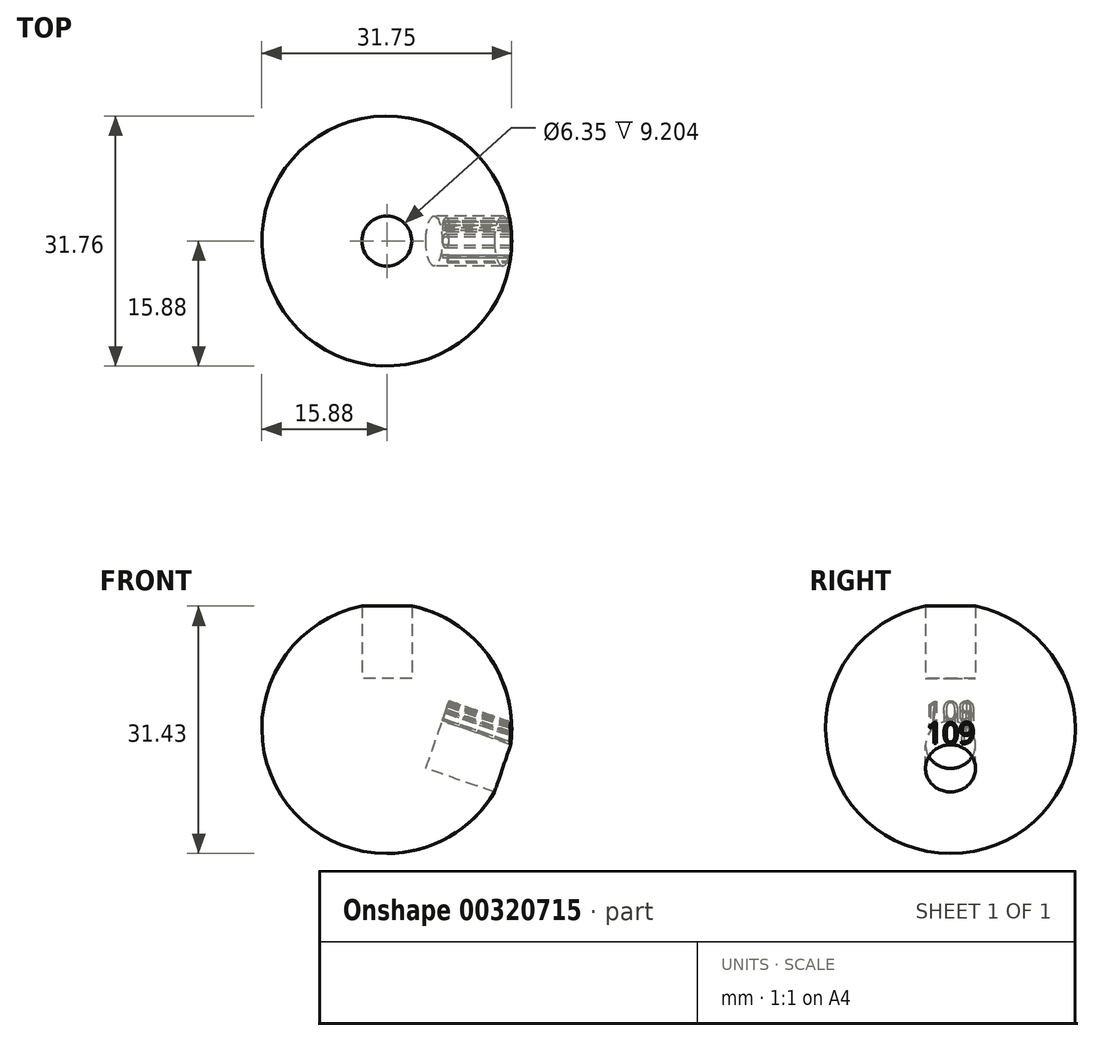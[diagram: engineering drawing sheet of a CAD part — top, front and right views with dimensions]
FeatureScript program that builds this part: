
annotation { "Feature Type Name" : "Feature", "Feature Type Description" : "" }
export const myFeature = defineFeature(function(context is Context, id is Id, definition is map)
    precondition{}
    {
        {
            var Q0;
            Q0=qCreatedBy(makeId("Front.planeOp"),FACE);
            var sketch = newSketch(context, id + "F0", { "sketchPlane" : qUnion([Q0])});
            skArc(sketch, "E0", {"start": v(0, 15.88) * mm, "mid": v(-15.88, 0) * mm, "end": v(0, -15.88) * mm});
            skLineSegment(sketch, "E1", {"start": v(0, 15.88) * mm, "end": v(0, -15.88) * mm});
            skSolve(sketch);
        }
        {
            var Q0;
            Q0=qCreatedBy(makeId("Top.planeOp"),FACE);
            var sketch = newSketch(context, id + "F1", { "sketchPlane" : qUnion([Q0])});
            skCircle(sketch, "E2", {"center": v(0, 0) * mm, "radius": 0.5 * mm});
            skCircle(sketch, "E3", {"center": v(0, 0) * mm, "radius": 15.88 * mm});
            skSolve(sketch);
        }
        {
            var Q0;
            Q0=makeQuery(id+"F0.imprint","IMPRINT",FACE,{"disambiguationData":[TD([[makeQuery(id+"F0.imprint","IMPRINT",EDGE,{"derivedFrom":sQuery(id+"F0.wireOp",EDGE,"E0")}),1.0]])]});
            var Q1;
            Q1=sQuery(id+"F1.wireOp",EDGE,"E3");
            revolve(context, id + "F2", {"entities" : qUnion([Q0]), "axis" : qUnion([Q1]), "revolveType" : RevolveType.FULL});
        }
        {
            var Q0;
            Q0=qCreatedBy(makeId("Top.planeOp"),FACE);
            cPlane(context, id + "F3", {"entities" : qUnion([Q0]), "cplaneType" : CPlaneType.OFFSET, "offset" : 6.35 * mm, "width" : 152.4 * mm, "height" : 152.4 * mm});
        }
        {
            var Q0;
            Q0=qCreatedBy(id+"F3.planeOp",FACE);
            var sketch = newSketch(context, id + "F4", { "sketchPlane" : qUnion([Q0])});
            skCircle(sketch, "E4", {"center": v(0, 0) * mm, "radius": 3.18 * mm});
            skSolve(sketch);
        }
        {
            var Q0;
            Q0=qSketchRegion(id+"F4",true);
            extrude(context, id + "F5", {"entities" : qUnion([Q0]), "depth" : 50.8 * mm});
        }
        {
            var Q0;
            Q0=qCreatedBy(makeId("Right.planeOp"),FACE);
            var sketch = newSketch(context, id + "F6", { "sketchPlane" : qUnion([Q0])});
            skLineSegment(sketch, "E5", {"start": v(0, 0) * mm, "end": v(-58.26, 0) * mm, "construction": true});
            skSolve(sketch);
        }
        {
            var Q0;
            Q0=makeQuery(id+"F5.opExtrude","SWEPT_BODY",BODY,{"disambiguationData":[OSD([sQuery(id+"F4.wireOp",EDGE,"E4")])]});
            var Q1;
            Q1=sQuery(id+"F6.wireOp",EDGE,"E5");
            transform(context, id + "F7", {"entities" : qUnion([Q0]), "transformType" : TransformType.ROTATION, "transformAxis" : qUnion([Q1]), "angle" : 109 * degree, "oppositeDirection" : true, "makeCopy" : true});
        }
        {
            var Q0;
            Q0=makeQuery(id+"F7.opPattern","COPY",FACE,{"derivedFrom":makeQuery(id+"F5.opExtrude","CAP_FACE",FACE,{"disambiguationData":[OSD([sQuery(id+"F4.wireOp",EDGE,"E4")])],"isStart":false}),"instanceName":"1"});
            cPlane(context, id + "F8", {"entities" : qUnion([Q0]), "cplaneType" : CPlaneType.OFFSET, "offset" : 31.75 * mm, "oppositeDirection" : true, "width" : 152.4 * mm, "height" : 152.4 * mm});
        }
        {
            var Q0;
            Q0=qCreatedBy(id+"F8.planeOp",FACE);
            var sketch = newSketch(context, id + "F9", { "sketchPlane" : qUnion([Q0])});
            skText(sketch, "E6", { "text": "109", "fontName": "OpenSans-Regular.ttf"});
            const initialGuessF9  = {"E6": [-0.00306, 0.0033, 1, 0, 0.00258]};
            skSetInitialGuess(sketch, initialGuessF9);
            skSolve(sketch);
        }
        {
            var Q0;
            Q0=qSketchRegion(id+"F9",true);
            extrude(context, id + "F10", {"entities" : qUnion([Q0]), "operationType" : NewBodyOperationType.REMOVE, "oppositeDirection" : true, "depth" : 19.05 * mm});
        }
        {
            var Q0;
            Q0=makeQuery(id+"F5.opExtrude","SWEPT_BODY",BODY,{"disambiguationData":[OSD([sQuery(id+"F4.wireOp",EDGE,"E4")])]});
            var Q1;
            Q1=makeQuery(id+"F7.opPattern","COPY",BODY,{"derivedFrom":makeQuery(id+"F5.opExtrude","SWEPT_BODY",BODY,{"disambiguationData":[OSD([sQuery(id+"F4.wireOp",EDGE,"E4")])]}),"instanceName":"1"});
            var Q2;
            Q2=makeQuery(id+"F2.opRevolve","SWEPT_BODY",BODY,{"disambiguationData":[OSD([sQuery(id+"F0.wireOp",EDGE,"E0"),sQuery(id+"F0.wireOp",EDGE,"E1")])]});
            booleanBodies(context, id + "F11", {"operationType" : BooleanOperationType.SUBTRACTION, "tools" : qUnion([Q0, Q1]), "targets" : qUnion([Q2])});
        }
    });
